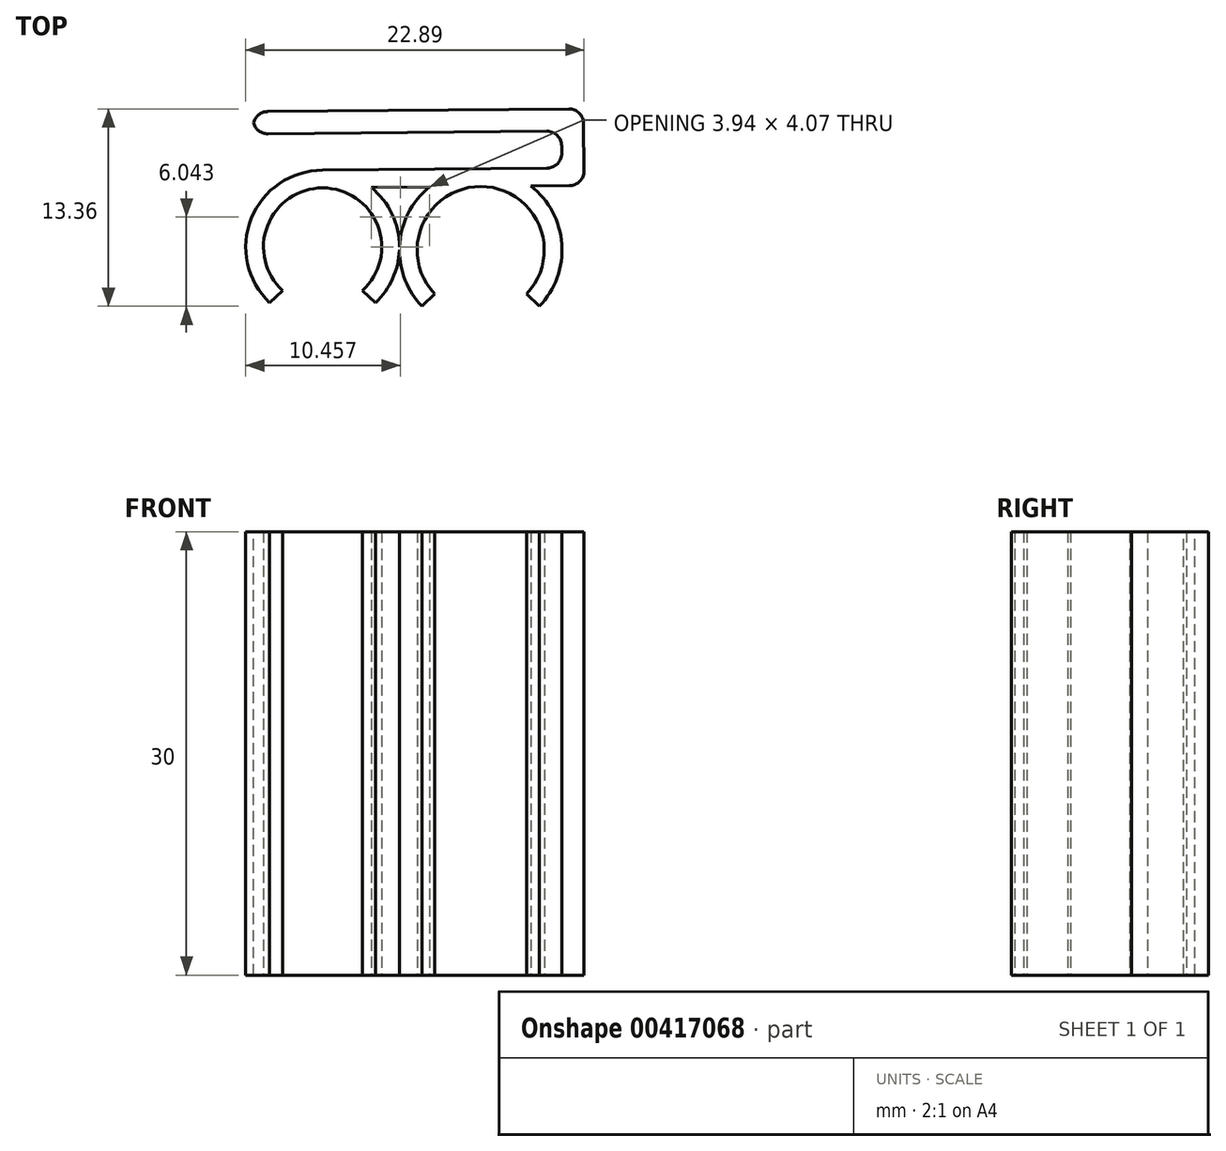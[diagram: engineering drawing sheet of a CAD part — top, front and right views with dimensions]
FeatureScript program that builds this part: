
annotation { "Feature Type Name" : "Feature", "Feature Type Description" : "" }
export const myFeature = defineFeature(function(context is Context, id is Id, definition is map)
    precondition{}
    {
        {
            var Q0;
            Q0=qCreatedBy(makeId("Top.planeOp"),FACE);
            var sketch = newSketch(context, id + "F0", { "sketchPlane" : qUnion([Q0])});
            skArc(sketch, "E0", {"start": v(2.7, -2.95) * mm, "mid": v(0, 4) * mm, "end": v(-2.7, -2.95) * mm});
            skArc(sketch, "E1.0", {"start": v(3.58, -3.77) * mm, "mid": v(0, 5.2) * mm, "end": v(-3.58, -3.77) * mm});
            skLineSegment(sketch, "E2", {"start": v(-2.7, -2.95) * mm, "end": v(-3.58, -3.77) * mm});
            skLineSegment(sketch, "E3.MirrorCS", {"start": v(2.7, -2.95) * mm, "end": v(3.58, -3.77) * mm});
            skArc(sketch, "E4", {"start": v(14.67, -4) * mm, "mid": v(10.7, 5.3) * mm, "end": v(6.72, -4) * mm});
            skPoint(sketch, "E4.first.point", {"position": v(5.2, 0) * mm});
            skPoint(sketch, "E4.second.point", {"position": v(9.67, 5.2) * mm});
            skPoint(sketch, "E4.third.point", {"position": v(16.2, 0) * mm});
            skArc(sketch, "E5.0", {"start": v(13.81, -3.16) * mm, "mid": v(10.7, 4.1) * mm, "end": v(7.58, -3.16) * mm});
            skLineSegment(sketch, "E6", {"start": v(7.58, -3.16) * mm, "end": v(6.72, -4) * mm});
            skLineSegment(sketch, "E7", {"start": v(10.7, -0.2) * mm, "end": v(10.7, -9.38) * mm, "construction": true});
            skLineSegment(sketch, "E8.MirrorCS", {"start": v(13.81, -3.16) * mm, "end": v(14.67, -4) * mm});
            skPoint(sketch, "E9.orphan", {"position": v(0, 5.2) * mm});
            skLineSegment(sketch, "E10", {"start": v(0, 5.2) * mm, "end": v(17.69, 5.36) * mm});
            skLineSegment(sketch, "E11.0", {"start": v(0.01, 4) * mm, "end": v(17.7, 4.16) * mm});
            skLineSegment(sketch, "E12.0", {"start": v(-0.02, 7.7) * mm, "end": v(17.66, 7.86) * mm});
            skLineSegment(sketch, "E13.0", {"start": v(-0.04, 9.2) * mm, "end": v(17.65, 9.36) * mm});
            skLineSegment(sketch, "E14", {"start": v(17.65, 9.36) * mm, "end": v(17.7, 4.16) * mm});
            skLineSegment(sketch, "E15", {"start": v(16.16, 7.85) * mm, "end": v(16.19, 5.35) * mm});
            skLineSegment(sketch, "E16", {"start": v(-0.02, 7.7) * mm, "end": v(-4.7, 7.66) * mm});
            skLineSegment(sketch, "E17.0", {"start": v(-0.04, 9.2) * mm, "end": v(-4.71, 9.16) * mm});
            skLineSegment(sketch, "E18", {"start": v(-4.71, 9.16) * mm, "end": v(-4.7, 7.66) * mm});
            skSolve(sketch);
        }
        {
            var Q0;
            Q0 = qSketchRegion(id + "F0", true);
            extrude(context, id + "F1", {"entities" : qUnion([Q0]), "depth" : 30 * mm, "offsetDistance" : 25 * mm});
        }
        {
            var Q0;
            Q0=makeQuery(id+"F1.opExtrude","SWEPT_EDGE",EDGE,{"disambiguationData":[OSD([sQuery(id+"F0.wireOp",EDGE,"E11.0"),sQuery(id+"F0.wireOp",EDGE,"E14")])]});
            var Q1;
            Q1=makeQuery(id+"F1.opExtrude","SWEPT_EDGE",EDGE,{"disambiguationData":[OSD([sQuery(id+"F0.wireOp",EDGE,"E13.0"),sQuery(id+"F0.wireOp",EDGE,"E14")])]});
            var Q2;
            Q2=makeQuery(id+"F1.opExtrude","SWEPT_EDGE",EDGE,{"disambiguationData":[OSD([sQuery(id+"F0.wireOp",EDGE,"E12.0"),sQuery(id+"F0.wireOp",EDGE,"E15")])]});
            var Q3;
            Q3=makeQuery(id+"F1.opExtrude","SWEPT_EDGE",EDGE,{"disambiguationData":[OSD([sQuery(id+"F0.wireOp",EDGE,"E10"),sQuery(id+"F0.wireOp",EDGE,"E15")])]});
            var Q4;
            Q4=makeQuery(id+"F1.opExtrude","SWEPT_EDGE",EDGE,{"disambiguationData":[OSD([sQuery(id+"F0.wireOp",EDGE,"E17.0"),sQuery(id+"F0.wireOp",EDGE,"E18")])]});
            var Q5;
            Q5=makeQuery(id+"F1.opExtrude","SWEPT_EDGE",EDGE,{"disambiguationData":[OSD([sQuery(id+"F0.wireOp",EDGE,"E16"),sQuery(id+"F0.wireOp",EDGE,"E18")])]});
            fillet(context, id + "F2", {"entities" : qUnion([Q0, Q1, Q2, Q3, Q4, Q5]), "radius" : 1 * mm, "tangentPropagation" : true, "allowEdgeOverflow" : false});
        }
    });
